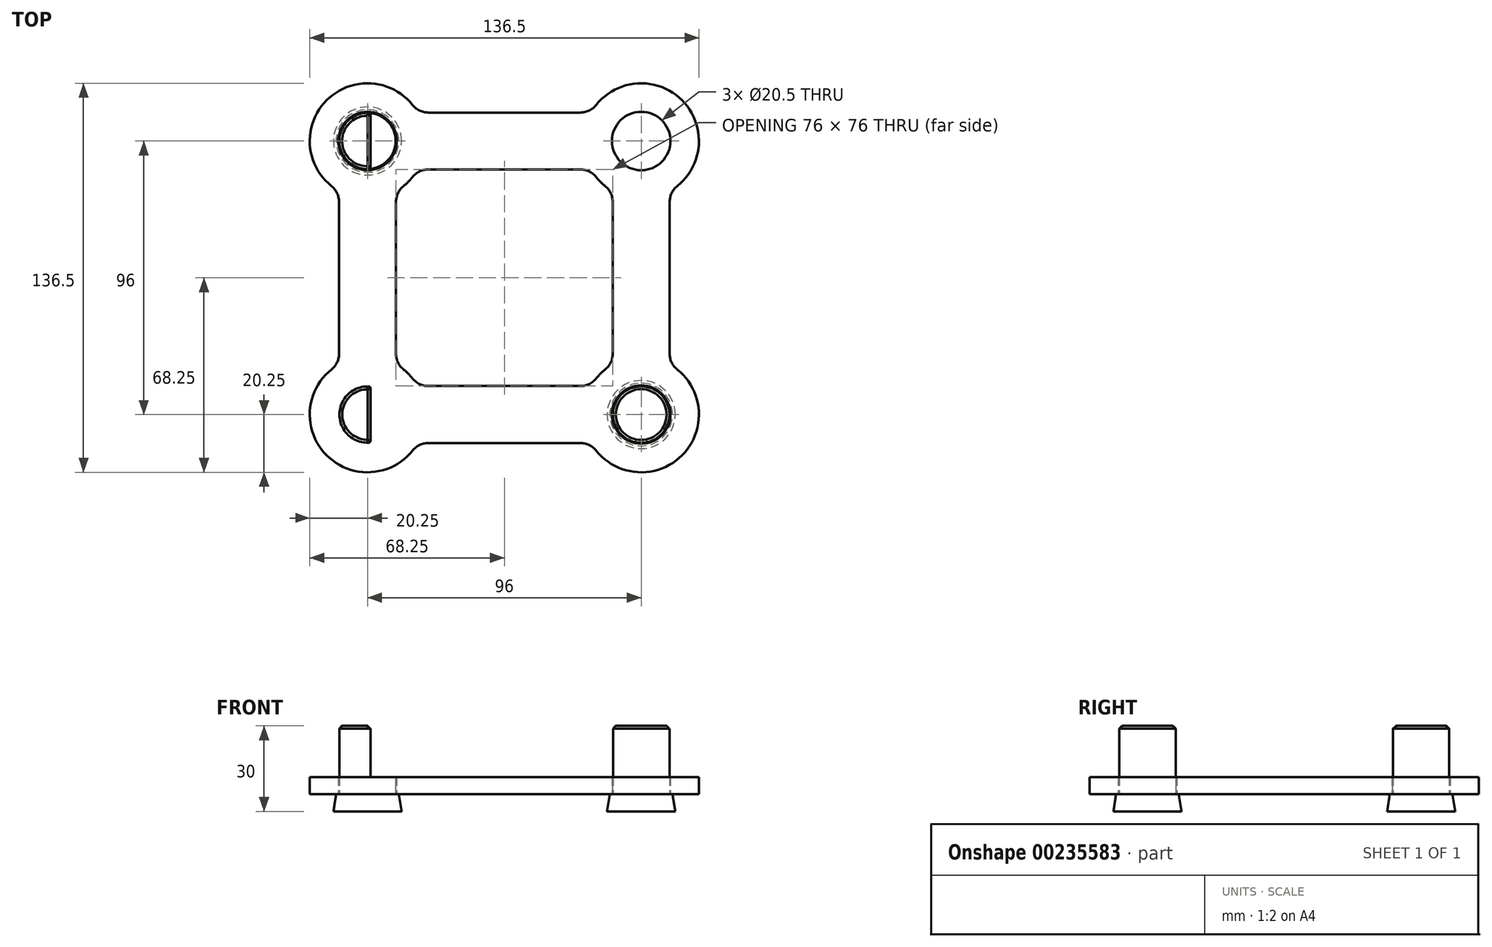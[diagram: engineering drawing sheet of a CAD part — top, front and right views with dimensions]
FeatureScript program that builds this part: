
annotation { "Feature Type Name" : "Feature", "Feature Type Description" : "" }
export const myFeature = defineFeature(function(context is Context, id is Id, definition is map)
    precondition{}
    {
        {
            var Q0;
            Q0=qCreatedBy(makeId("Top.planeOp"),FACE);
            var sketch = newSketch(context, id + "F0", { "sketchPlane" : qUnion([Q0])});
            skCircle(sketch, "E0", {"center": v(0, 0) * mm, "radius": 10.25 * mm, "construction": true});
            skCircle(sketch, "E1.0.1.0", {"center": v(0, 96) * mm, "radius": 10.25 * mm});
            skCircle(sketch, "E1.1.0.0", {"center": v(96, 0) * mm, "radius": 10.25 * mm});
            skCircle(sketch, "E1.1.1.0", {"center": v(96, 96) * mm, "radius": 10.25 * mm});
            skLineSegment(sketch, "E1.direction1", {"start": v(0, 0) * mm, "end": v(96, 0) * mm, "construction": true});
            skLineSegment(sketch, "E1.direction2", {"start": v(0, 0) * mm, "end": v(0, 96) * mm, "construction": true});
            skArc(sketch, "E2.0", {"start": v(-10, 17.6) * mm, "mid": v(-14.32, -14.32) * mm, "end": v(17.6, -10) * mm});
            skLineSegment(sketch, "E3", {"start": v(96, 0) * mm, "end": v(0, 96) * mm, "construction": true});
            skLineSegment(sketch, "E4.trimOffspring", {"start": v(-10, 17.6) * mm, "end": v(-10, 78.4) * mm});
            skLineSegment(sketch, "E5.trimOffspring", {"start": v(10, 17.6) * mm, "end": v(10, 78.4) * mm});
            skArc(sketch, "E6.1.0", {"start": v(78.4, -10) * mm, "mid": v(110.32, -14.32) * mm, "end": v(106, 17.6) * mm});
            skLineSegment(sketch, "E6.1.1", {"start": v(78.4, 10) * mm, "end": v(17.6, 10) * mm});
            skLineSegment(sketch, "E6.1.2", {"start": v(78.4, -10) * mm, "end": v(17.6, -10) * mm});
            skArc(sketch, "E6.2.0", {"start": v(106, 78.4) * mm, "mid": v(110.32, 110.32) * mm, "end": v(78.4, 106) * mm});
            skLineSegment(sketch, "E6.2.1", {"start": v(86, 78.4) * mm, "end": v(86, 17.6) * mm});
            skLineSegment(sketch, "E6.2.2", {"start": v(106, 78.4) * mm, "end": v(106, 17.6) * mm});
            skArc(sketch, "E6.3.0", {"start": v(17.6, 106) * mm, "mid": v(-14.32, 110.32) * mm, "end": v(-10, 78.4) * mm});
            skLineSegment(sketch, "E6.3.1", {"start": v(17.6, 86) * mm, "end": v(78.4, 86) * mm});
            skLineSegment(sketch, "E6.3.2", {"start": v(17.6, 106) * mm, "end": v(78.4, 106) * mm});
            skPoint(sketch, "E6.center", {"position": v(48, 48) * mm});
            skArc(sketch, "E7.trimOffspring", {"start": v(78.4, 86) * mm, "mid": v(81.68, 81.68) * mm, "end": v(86, 78.4) * mm});
            skArc(sketch, "E8.trimOffspring", {"start": v(86, 17.6) * mm, "mid": v(81.68, 14.32) * mm, "end": v(78.4, 10) * mm});
            skArc(sketch, "E9.trimOffspring", {"start": v(17.6, 10) * mm, "mid": v(14.32, 14.32) * mm, "end": v(10, 17.6) * mm});
            skArc(sketch, "E10", {"start": v(10, 78.4) * mm, "mid": v(14.31, 81.69) * mm, "end": v(17.6, 86) * mm});
            skSolve(sketch);
        }
        {
            var Q0;
            Q0 = qSketchRegion(id + "F0", true);
            extrude(context, id + "F1", {"entities" : qUnion([Q0]), "depth" : 6 * mm});
        }
        {
            var Q0;
            Q0=makeQuery(id+"F1.opExtrude","CAP_FACE",FACE,{"disambiguationData":[OSD([sQuery(id+"F0.wireOp",EDGE,"E1.0.1.0"),sQuery(id+"F0.wireOp",EDGE,"E1.1.0.0"),sQuery(id+"F0.wireOp",EDGE,"E1.1.1.0"),sQuery(id+"F0.wireOp",EDGE,"E2.0"),sQuery(id+"F0.wireOp",EDGE,"E4.trimOffspring"),sQuery(id+"F0.wireOp",EDGE,"E5.trimOffspring"),sQuery(id+"F0.wireOp",EDGE,"E6.1.0"),sQuery(id+"F0.wireOp",EDGE,"E6.1.1"),sQuery(id+"F0.wireOp",EDGE,"E6.1.2"),sQuery(id+"F0.wireOp",EDGE,"E6.2.0"),sQuery(id+"F0.wireOp",EDGE,"E6.2.1"),sQuery(id+"F0.wireOp",EDGE,"E6.2.2"),sQuery(id+"F0.wireOp",EDGE,"E6.3.0"),sQuery(id+"F0.wireOp",EDGE,"E6.3.1"),sQuery(id+"F0.wireOp",EDGE,"E6.3.2"),sQuery(id+"F0.wireOp",EDGE,"E7.trimOffspring"),sQuery(id+"F0.wireOp",EDGE,"E8.trimOffspring"),sQuery(id+"F0.wireOp",EDGE,"E9.trimOffspring"),sQuery(id+"F0.wireOp",EDGE,"E10")])],"isStart":false});
            var sketch = newSketch(context, id + "F2", { "sketchPlane" : qUnion([Q0])});
            skArc(sketch, "E11", {"start": v(1, 9.8) * mm, "mid": v(-9.85, 0) * mm, "end": v(1, -9.8) * mm});
            skLineSegment(sketch, "E12", {"start": v(1, 9.8) * mm, "end": v(1, -9.8) * mm});
            skSolve(sketch);
        }
        {
            var Q0;
            Q0 = qSketchRegion(id + "F2", true);
            extrude(context, id + "F3", {"entities" : qUnion([Q0]), "operationType" : NewBodyOperationType.ADD, "depth" : 18 * mm});
        }
        {
            var Q0;
            Q0=makeQuery(id+"F1.opExtrude","SWEPT_EDGE",EDGE,{"disambiguationData":[OSD([sQuery(id+"F0.wireOp",EDGE,"E5.trimOffspring"),sQuery(id+"F0.wireOp",EDGE,"E10")])]});
            var Q1;
            Q1=makeQuery(id+"F1.opExtrude","SWEPT_EDGE",EDGE,{"disambiguationData":[OSD([sQuery(id+"F0.wireOp",EDGE,"E6.3.1"),sQuery(id+"F0.wireOp",EDGE,"E10")])]});
            var Q2;
            Q2=makeQuery(id+"F1.opExtrude","SWEPT_EDGE",EDGE,{"disambiguationData":[OSD([sQuery(id+"F0.wireOp",EDGE,"E6.2.0"),sQuery(id+"F0.wireOp",EDGE,"E6.2.2")])]});
            var Q3;
            Q3=makeQuery(id+"F1.opExtrude","SWEPT_EDGE",EDGE,{"disambiguationData":[OSD([sQuery(id+"F0.wireOp",EDGE,"E2.0"),sQuery(id+"F0.wireOp",EDGE,"E6.1.2")])]});
            var Q4;
            Q4=makeQuery(id+"F1.opExtrude","SWEPT_EDGE",EDGE,{"disambiguationData":[OSD([sQuery(id+"F0.wireOp",EDGE,"E6.1.0"),sQuery(id+"F0.wireOp",EDGE,"E6.2.2")])]});
            var Q5;
            Q5=makeQuery(id+"F1.opExtrude","SWEPT_EDGE",EDGE,{"disambiguationData":[OSD([sQuery(id+"F0.wireOp",EDGE,"E6.1.1"),sQuery(id+"F0.wireOp",EDGE,"E9.trimOffspring")])]});
            var Q6;
            Q6=makeQuery(id+"F1.opExtrude","SWEPT_EDGE",EDGE,{"disambiguationData":[OSD([sQuery(id+"F0.wireOp",EDGE,"E5.trimOffspring"),sQuery(id+"F0.wireOp",EDGE,"E9.trimOffspring")])]});
            var Q7;
            Q7=makeQuery(id+"F1.opExtrude","SWEPT_EDGE",EDGE,{"disambiguationData":[OSD([sQuery(id+"F0.wireOp",EDGE,"E6.2.0"),sQuery(id+"F0.wireOp",EDGE,"E6.3.2")])]});
            var Q8;
            Q8=makeQuery(id+"F1.opExtrude","SWEPT_EDGE",EDGE,{"disambiguationData":[OSD([sQuery(id+"F0.wireOp",EDGE,"E6.3.0"),sQuery(id+"F0.wireOp",EDGE,"E6.3.2")])]});
            var Q9;
            Q9=makeQuery(id+"F1.opExtrude","SWEPT_EDGE",EDGE,{"disambiguationData":[OSD([sQuery(id+"F0.wireOp",EDGE,"E6.2.1"),sQuery(id+"F0.wireOp",EDGE,"E8.trimOffspring")])]});
            var Q10;
            Q10=makeQuery(id+"F1.opExtrude","SWEPT_EDGE",EDGE,{"disambiguationData":[OSD([sQuery(id+"F0.wireOp",EDGE,"E6.1.1"),sQuery(id+"F0.wireOp",EDGE,"E8.trimOffspring")])]});
            var Q11;
            Q11=makeQuery(id+"F1.opExtrude","SWEPT_EDGE",EDGE,{"disambiguationData":[OSD([sQuery(id+"F0.wireOp",EDGE,"E2.0"),sQuery(id+"F0.wireOp",EDGE,"E4.trimOffspring")])]});
            var Q12;
            Q12=makeQuery(id+"F1.opExtrude","SWEPT_EDGE",EDGE,{"disambiguationData":[OSD([sQuery(id+"F0.wireOp",EDGE,"E4.trimOffspring"),sQuery(id+"F0.wireOp",EDGE,"E6.3.0")])]});
            var Q13;
            Q13=makeQuery(id+"F1.opExtrude","SWEPT_EDGE",EDGE,{"disambiguationData":[OSD([sQuery(id+"F0.wireOp",EDGE,"E6.3.1"),sQuery(id+"F0.wireOp",EDGE,"E7.trimOffspring")])]});
            var Q14;
            Q14=makeQuery(id+"F1.opExtrude","SWEPT_EDGE",EDGE,{"disambiguationData":[OSD([sQuery(id+"F0.wireOp",EDGE,"E6.1.0"),sQuery(id+"F0.wireOp",EDGE,"E6.1.2")])]});
            var Q15;
            Q15=makeQuery(id+"F1.opExtrude","SWEPT_EDGE",EDGE,{"disambiguationData":[OSD([sQuery(id+"F0.wireOp",EDGE,"E6.2.1"),sQuery(id+"F0.wireOp",EDGE,"E7.trimOffspring")])]});
            fillet(context, id + "F4", {"entities" : qUnion([Q0, Q1, Q2, Q3, Q4, Q5, Q6, Q7, Q8, Q9, Q10, Q11, Q12, Q13, Q14, Q15]), "radius" : 7 * mm, "tangentPropagation" : true, "allowEdgeOverflow" : false});
        }
        {
            var Q0;
            Q0=makeQuery(id+"F3.opExtrude","CAP_EDGE",EDGE,{"disambiguationData":[OSD([sQuery(id+"F2.wireOp",EDGE,"E11")])],"isStart":false});
            var Q1;
            Q1=makeQuery(id+"F3.opExtrude","CAP_EDGE",EDGE,{"disambiguationData":[OSD([sQuery(id+"F2.wireOp",EDGE,"E12")])],"isStart":false});
            chamfer(context, id + "F5", {"entities" : qUnion([Q0, Q1]), "width" : 1 * mm, "tangentPropagation" : true});
        }
        {
            var Q0;
            {var subQ0=sQuery(id+"F2.wireOp",EDGE,"E12");var subQ1=sQuery(id+"F2.wireOp",EDGE,"E11");Q0=makeQuery(id+"F3.opExtrude","SWEPT_EDGE",EDGE,{"disambiguationData":[OSD([subQ1,subQ0]),TDD([makeQuery(id+"F2.imprint","INTERSECT",VERTEX,{"disambiguationData":[OD(0.0)],"derivedFrom":[subQ1,subQ0]})])]});}
            var Q1;
            {var subQ0=sQuery(id+"F2.wireOp",EDGE,"E12");var subQ1=sQuery(id+"F2.wireOp",EDGE,"E11");Q1=makeQuery(id+"F3.opExtrude","SWEPT_EDGE",EDGE,{"disambiguationData":[OSD([subQ1,subQ0]),TDD([makeQuery(id+"F2.imprint","INTERSECT",VERTEX,{"disambiguationData":[OD(1.0)],"derivedFrom":[subQ1,subQ0]})])]});}
            var Q2;
            Q2=makeQuery(id+"F5.opChamfer","BLEND_EDGE",EDGE,{"disambiguationData":[OD(1.0)],"blendedFrom":[makeQuery(id+"F3.opExtrude","CAP_EDGE",EDGE,{"disambiguationData":[OSD([sQuery(id+"F2.wireOp",EDGE,"E11")])],"isStart":false}),makeQuery(id+"F3.opExtrude","CAP_EDGE",EDGE,{"disambiguationData":[OSD([sQuery(id+"F2.wireOp",EDGE,"E12")])],"isStart":false})],"blendedInto":[]});
            var Q3;
            Q3=makeQuery(id+"F5.opChamfer","BLEND_EDGE",EDGE,{"disambiguationData":[OD(0.0)],"blendedFrom":[makeQuery(id+"F3.opExtrude","CAP_EDGE",EDGE,{"disambiguationData":[OSD([sQuery(id+"F2.wireOp",EDGE,"E11")])],"isStart":false}),makeQuery(id+"F3.opExtrude","CAP_EDGE",EDGE,{"disambiguationData":[OSD([sQuery(id+"F2.wireOp",EDGE,"E12")])],"isStart":false})],"blendedInto":[]});
            fillet(context, id + "F6", {"entities" : qUnion([Q0, Q1, Q2, Q3]), "radius" : 0.5 * mm, "tangentPropagation" : true, "allowEdgeOverflow" : false});
        }
        {
            var Q0;
            Q0=makeQuery(id+"F1.opExtrude","CAP_FACE",FACE,{"disambiguationData":[OSD([sQuery(id+"F0.wireOp",EDGE,"E1.0.1.0"),sQuery(id+"F0.wireOp",EDGE,"E1.1.0.0"),sQuery(id+"F0.wireOp",EDGE,"E1.1.1.0"),sQuery(id+"F0.wireOp",EDGE,"E2.0"),sQuery(id+"F0.wireOp",EDGE,"E4.trimOffspring"),sQuery(id+"F0.wireOp",EDGE,"E5.trimOffspring"),sQuery(id+"F0.wireOp",EDGE,"E6.1.0"),sQuery(id+"F0.wireOp",EDGE,"E6.1.1"),sQuery(id+"F0.wireOp",EDGE,"E6.1.2"),sQuery(id+"F0.wireOp",EDGE,"E6.2.0"),sQuery(id+"F0.wireOp",EDGE,"E6.2.1"),sQuery(id+"F0.wireOp",EDGE,"E6.2.2"),sQuery(id+"F0.wireOp",EDGE,"E6.3.0"),sQuery(id+"F0.wireOp",EDGE,"E6.3.1"),sQuery(id+"F0.wireOp",EDGE,"E6.3.2"),sQuery(id+"F0.wireOp",EDGE,"E7.trimOffspring"),sQuery(id+"F0.wireOp",EDGE,"E8.trimOffspring"),sQuery(id+"F0.wireOp",EDGE,"E9.trimOffspring"),sQuery(id+"F0.wireOp",EDGE,"E10")])],"isStart":true});
            var sketch = newSketch(context, id + "F7", { "sketchPlane" : qUnion([Q0])});
            skCircle(sketch, "E13", {"center": v(0, -96) * mm, "radius": 11 * mm});
            skSolve(sketch);
        }
        {
            var Q0;
            Q0 = qSketchRegion(id + "F7", true);
            extrude(context, id + "F8", {"entities" : qUnion([Q0]), "depth" : 6 * mm, "hasDraft" : true, "draftAngle" : 9 * degree});
        }
        {
            var Q0;
            Q0=makeQuery(id+"F8.opExtrude","CAP_FACE",FACE,{"disambiguationData":[OSD([sQuery(id+"F7.wireOp",EDGE,"E13")])],"isStart":true});
            var sketch = newSketch(context, id + "F9", { "sketchPlane" : qUnion([Q0])});
            skCircle(sketch, "E14", {"center": v(0, 96) * mm, "radius": 9.85 * mm});
            skSolve(sketch);
        }
        {
            var Q0;
            Q0 = qSketchRegion(id + "F9", true);
            extrude(context, id + "F10", {"entities" : qUnion([Q0]), "operationType" : NewBodyOperationType.ADD, "depth" : 6 * mm});
        }
        {
            var Q0;
            Q0=makeQuery(id+"F10.opExtrude","CAP_FACE",FACE,{"disambiguationData":[OSD([sQuery(id+"F9.wireOp",EDGE,"E14")])],"isStart":false});
            var sketch = newSketch(context, id + "F11", { "sketchPlane" : qUnion([Q0])});
            skLineSegment(sketch, "E15", {"start": v(1, 105.8) * mm, "end": v(1, 86.2) * mm});
            skArc(sketch, "E16", {"start": v(1, 105.8) * mm, "mid": v(-9.92, 96) * mm, "end": v(1, 86.2) * mm});
            skSolve(sketch);
        }
        {
            var Q0;
            Q0 = qSketchRegion(id + "F11", true);
            extrude(context, id + "F12", {"entities" : qUnion([Q0]), "operationType" : NewBodyOperationType.ADD, "depth" : 18 * mm});
        }
        {
            var Q0;
            Q0=makeQuery(id+"F12.opExtrude","CAP_EDGE",EDGE,{"disambiguationData":[OSD([sQuery(id+"F11.wireOp",EDGE,"E16")])],"isStart":false});
            var Q1;
            Q1=makeQuery(id+"F12.opExtrude","CAP_EDGE",EDGE,{"disambiguationData":[OSD([sQuery(id+"F11.wireOp",EDGE,"E15")])],"isStart":false});
            chamfer(context, id + "F13", {"entities" : qUnion([Q0, Q1]), "width" : 1 * mm, "tangentPropagation" : true});
        }
        {
            var Q0;
            {var subQ0=sQuery(id+"F11.wireOp",EDGE,"E16");var subQ1=sQuery(id+"F11.wireOp",EDGE,"E15");var subQ2=sQuery(id+"F9.wireOp",EDGE,"E14");Q0=makeQuery(id+"F12.boolean.opBoolean","SPLIT",EDGE,{"disambiguationData":[TD([makeQuery(id+"F12.opExtrude","CAP_FACE",FACE,{"disambiguationData":[OSD([subQ1,subQ0])],"isStart":false})])],"derivedFrom":makeQuery(id+"F12.opExtrude","SWEPT_EDGE",EDGE,{"disambiguationData":[OSD([subQ2,subQ1,subQ0]),TDD([makeQuery(id+"F11.imprint","INTERSECT",VERTEX,{"disambiguationData":[OD(1.0)],"derivedFrom":[makeQuery(id+"F10.opExtrude","CAP_EDGE",EDGE,{"disambiguationData":[OSD([subQ2])],"isStart":true}),subQ1,subQ0]})])]})});}
            var Q1;
            {var subQ0=sQuery(id+"F11.wireOp",EDGE,"E16");var subQ1=sQuery(id+"F11.wireOp",EDGE,"E15");var subQ2=sQuery(id+"F9.wireOp",EDGE,"E14");Q1=makeQuery(id+"F12.boolean.opBoolean","SPLIT",EDGE,{"disambiguationData":[TD([makeQuery(id+"F12.opExtrude","CAP_FACE",FACE,{"disambiguationData":[OSD([subQ1,subQ0])],"isStart":false})])],"derivedFrom":makeQuery(id+"F12.opExtrude","SWEPT_EDGE",EDGE,{"disambiguationData":[OSD([subQ2,subQ1,subQ0]),TDD([makeQuery(id+"F11.imprint","INTERSECT",VERTEX,{"disambiguationData":[OD(0.0)],"derivedFrom":[makeQuery(id+"F10.opExtrude","CAP_EDGE",EDGE,{"disambiguationData":[OSD([subQ2])],"isStart":true}),subQ1,subQ0]})])]})});}
            var Q2;
            Q2=makeQuery(id+"F13.opChamfer","BLEND_EDGE",EDGE,{"disambiguationData":[OD(1.0)],"blendedFrom":[makeQuery(id+"F12.opExtrude","CAP_EDGE",EDGE,{"disambiguationData":[OSD([sQuery(id+"F11.wireOp",EDGE,"E15")])],"isStart":false}),makeQuery(id+"F12.opExtrude","CAP_EDGE",EDGE,{"disambiguationData":[OSD([sQuery(id+"F11.wireOp",EDGE,"E16")])],"isStart":false})],"blendedInto":[]});
            var Q3;
            Q3=makeQuery(id+"F13.opChamfer","BLEND_EDGE",EDGE,{"disambiguationData":[OD(0.0)],"blendedFrom":[makeQuery(id+"F12.opExtrude","CAP_EDGE",EDGE,{"disambiguationData":[OSD([sQuery(id+"F11.wireOp",EDGE,"E15")])],"isStart":false}),makeQuery(id+"F12.opExtrude","CAP_EDGE",EDGE,{"disambiguationData":[OSD([sQuery(id+"F11.wireOp",EDGE,"E16")])],"isStart":false})],"blendedInto":[]});
            fillet(context, id + "F14", {"entities" : qUnion([Q0, Q1, Q2, Q3]), "radius" : 0.5 * mm, "tangentPropagation" : true, "allowEdgeOverflow" : false});
        }
        {
            var Q0;
            Q0=qCreatedBy(makeId("Top.planeOp"),FACE);
            var sketch = newSketch(context, id + "F15", { "sketchPlane" : qUnion([Q0])});
            skCircle(sketch, "E17", {"center": v(96, 0) * mm, "radius": 11 * mm});
            skSolve(sketch);
        }
        {
            var Q0;
            Q0 = qSketchRegion(id + "F15", true);
            extrude(context, id + "F16", {"entities" : qUnion([Q0]), "oppositeDirection" : true, "depth" : 6 * mm, "hasDraft" : true, "draftAngle" : 9 * degree});
        }
        {
            var Q0;
            Q0=makeQuery(id+"F16.opExtrude","CAP_FACE",FACE,{"disambiguationData":[OSD([sQuery(id+"F15.wireOp",EDGE,"E17")])],"isStart":true});
            var sketch = newSketch(context, id + "F17", { "sketchPlane" : qUnion([Q0])});
            skCircle(sketch, "E18", {"center": v(96, 0) * mm, "radius": 9.9 * mm});
            skSolve(sketch);
        }
        {
            var Q0;
            Q0 = qSketchRegion(id + "F17", true);
            extrude(context, id + "F18", {"entities" : qUnion([Q0]), "operationType" : NewBodyOperationType.ADD, "depth" : 24 * mm});
        }
        {
            var Q0;
            Q0=makeQuery(id+"F18.opExtrude","CAP_FACE",FACE,{"disambiguationData":[OSD([sQuery(id+"F17.wireOp",EDGE,"E18")])],"isStart":false});
            chamfer(context, id + "F19", {"entities" : qUnion([Q0]), "width" : 1 * mm, "tangentPropagation" : true});
        }
    });
